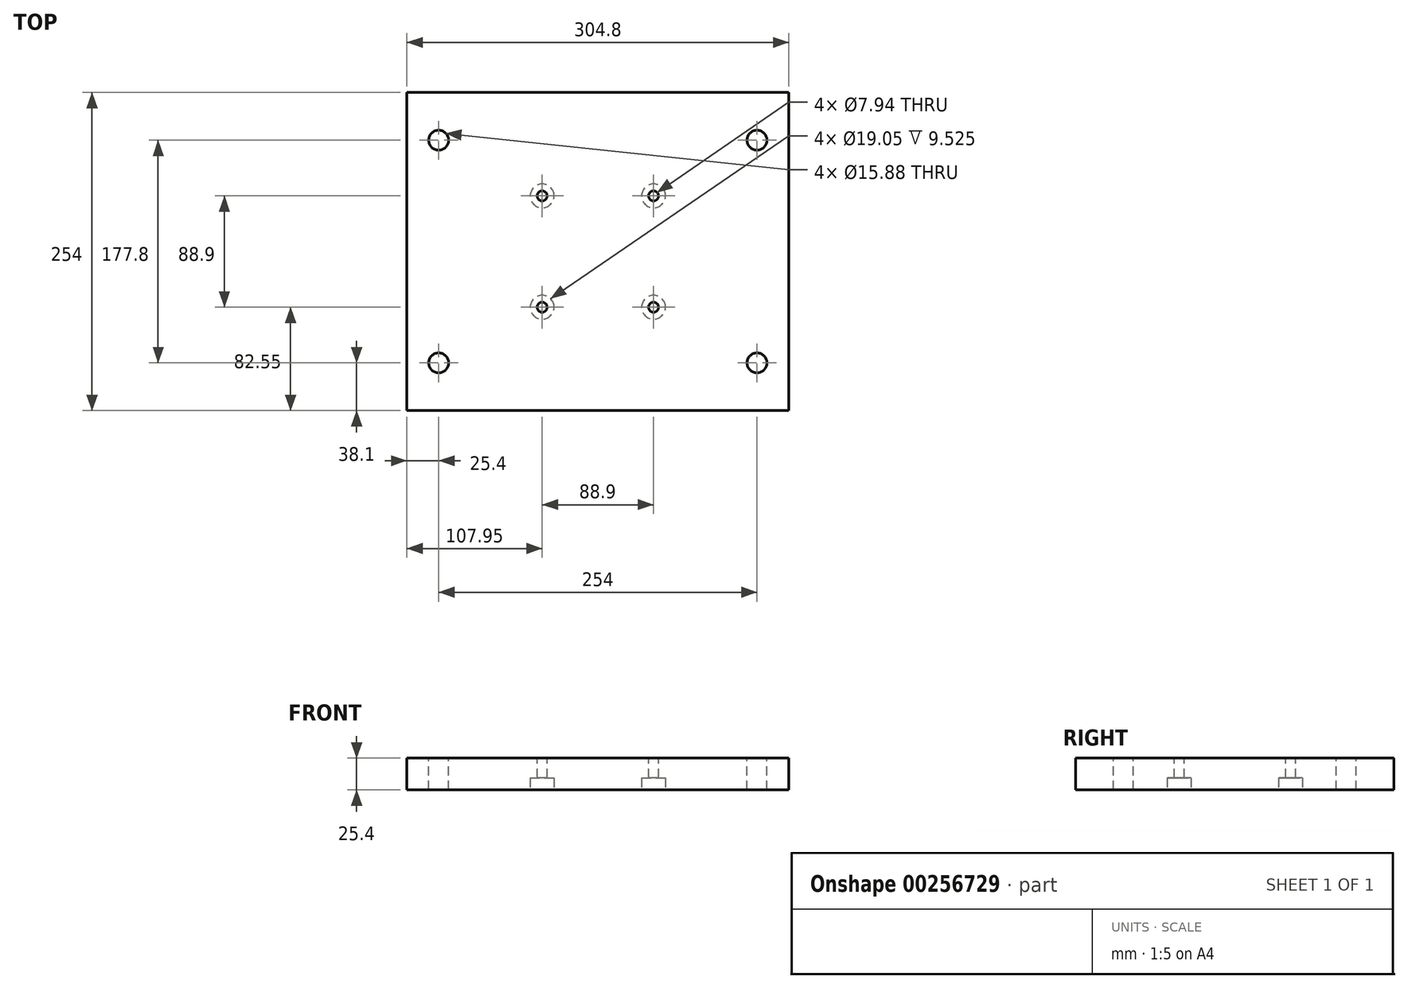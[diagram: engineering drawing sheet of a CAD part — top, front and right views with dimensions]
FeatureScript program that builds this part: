
annotation { "Feature Type Name" : "Feature", "Feature Type Description" : "" }
export const myFeature = defineFeature(function(context is Context, id is Id, definition is map)
    precondition{}
    {
        {
            var Q0;
            Q0=qCreatedBy(makeId("Top.planeOp"),FACE);
            var sketch = newSketch(context, id + "F0", { "sketchPlane" : qUnion([Q0])});
            skLineSegment(sketch, "E0.bottom", {"start": v(0, 0) * mm, "end": v(304.8, 0) * mm});
            skLineSegment(sketch, "E0.top", {"start": v(0, 254) * mm, "end": v(304.8, 254) * mm});
            skLineSegment(sketch, "E0.left", {"start": v(0, 0) * mm, "end": v(0, 254) * mm});
            skLineSegment(sketch, "E0.right", {"start": v(304.8, 0) * mm, "end": v(304.8, 254) * mm});
            skSolve(sketch);
        }
        {
            var Q0;
            Q0=makeQuery(id+"F0.imprint","IMPRINT",FACE,{"disambiguationData":[TD([[makeQuery(id+"F0.imprint","IMPRINT",EDGE,{"derivedFrom":sQuery(id+"F0.wireOp",EDGE,"E0.bottom")}),1.0]])]});
            extrude(context, id + "F1", {"entities" : qUnion([Q0]), "oppositeDirection" : true, "depth" : 25.4 * mm});
        }
        {
            var Q0;
            Q0=makeQuery(id+"F1.opExtrude","CAP_FACE",FACE,{"disambiguationData":[OSD([sQuery(id+"F0.wireOp",EDGE,"E0.bottom"),sQuery(id+"F0.wireOp",EDGE,"E0.top"),sQuery(id+"F0.wireOp",EDGE,"E0.left"),sQuery(id+"F0.wireOp",EDGE,"E0.right")])],"isStart":true});
            var sketch = newSketch(context, id + "F2", { "sketchPlane" : qUnion([Q0])});
            skLineSegment(sketch, "E1.bottom", {"start": v(196.85, 171.45) * mm, "end": v(107.95, 171.45) * mm, "construction": true});
            skLineSegment(sketch, "E1.top", {"start": v(196.85, 82.55) * mm, "end": v(107.95, 82.55) * mm, "construction": true});
            skLineSegment(sketch, "E1.left", {"start": v(196.85, 171.45) * mm, "end": v(196.85, 82.55) * mm, "construction": true});
            skLineSegment(sketch, "E1.right", {"start": v(107.95, 171.45) * mm, "end": v(107.95, 82.55) * mm, "construction": true});
            skPoint(sketch, "E1.middle", {"position": v(152.4, 127) * mm});
            skCircle(sketch, "E2", {"center": v(107.95, 171.45) * mm, "radius": 3.97 * mm});
            skCircle(sketch, "E3", {"center": v(196.85, 171.45) * mm, "radius": 3.97 * mm});
            skCircle(sketch, "E4", {"center": v(107.95, 82.55) * mm, "radius": 3.97 * mm});
            skCircle(sketch, "E5", {"center": v(196.85, 82.55) * mm, "radius": 3.97 * mm});
            skPoint(sketch, "E6.endSnap0", {"position": v(152.4, 0) * mm});
            skLineSegment(sketch, "E7", {"start": v(0, 254) * mm, "end": v(304.8, 0) * mm, "construction": true});
            skLineSegment(sketch, "E8", {"start": v(304.8, 0) * mm, "end": v(304.8, 254) * mm, "construction": true});
            skLineSegment(sketch, "E9", {"start": v(304.8, 254) * mm, "end": v(0, 0) * mm, "construction": true});
            skLineSegment(sketch, "E10", {"start": v(152.4, 254) * mm, "end": v(152.4, 0) * mm, "construction": true});
            skLineSegment(sketch, "E11", {"start": v(0, 127) * mm, "end": v(304.8, 127) * mm, "construction": true});
            skLineSegment(sketch, "E12.bottom", {"start": v(279.4, 38.1) * mm, "end": v(25.4, 38.1) * mm, "construction": true});
            skLineSegment(sketch, "E12.top", {"start": v(279.4, 215.9) * mm, "end": v(25.4, 215.9) * mm, "construction": true});
            skLineSegment(sketch, "E12.left", {"start": v(279.4, 38.1) * mm, "end": v(279.4, 215.9) * mm, "construction": true});
            skLineSegment(sketch, "E12.right", {"start": v(25.4, 38.1) * mm, "end": v(25.4, 215.9) * mm, "construction": true});
            skCircle(sketch, "E13", {"center": v(25.4, 215.9) * mm, "radius": 7.94 * mm});
            skCircle(sketch, "E14", {"center": v(279.4, 215.9) * mm, "radius": 7.94 * mm});
            skCircle(sketch, "E15", {"center": v(279.4, 38.1) * mm, "radius": 7.94 * mm});
            skCircle(sketch, "E16", {"center": v(25.4, 38.1) * mm, "radius": 7.94 * mm});
            skSolve(sketch);
        }
        {
            var Q0;
            Q0=makeQuery(id+"F2.imprint","IMPRINT",FACE,{"disambiguationData":[TD([[makeQuery(id+"F2.imprint","IMPRINT",EDGE,{"derivedFrom":sQuery(id+"F2.wireOp",EDGE,"E2")}),1.0]])]});
            var Q1;
            Q1=makeQuery(id+"F2.imprint","IMPRINT",FACE,{"disambiguationData":[TD([[makeQuery(id+"F2.imprint","IMPRINT",EDGE,{"derivedFrom":sQuery(id+"F2.wireOp",EDGE,"E3")}),1.0]])]});
            var Q2;
            Q2=makeQuery(id+"F2.imprint","IMPRINT",FACE,{"disambiguationData":[TD([[makeQuery(id+"F2.imprint","IMPRINT",EDGE,{"derivedFrom":sQuery(id+"F2.wireOp",EDGE,"E5")}),1.0]])]});
            var Q3;
            Q3=makeQuery(id+"F2.imprint","IMPRINT",FACE,{"disambiguationData":[TD([[makeQuery(id+"F2.imprint","IMPRINT",EDGE,{"derivedFrom":sQuery(id+"F2.wireOp",EDGE,"E4")}),1.0]])]});
            extrude(context, id + "F3", {"entities" : qUnion([Q0, Q1, Q2, Q3]), "operationType" : NewBodyOperationType.REMOVE, "oppositeDirection" : true, "depth" : 25.4 * mm});
        }
        {
            var Q0;
            Q0=makeQuery(id+"F1.opExtrude","CAP_FACE",FACE,{"disambiguationData":[OSD([sQuery(id+"F0.wireOp",EDGE,"E0.bottom"),sQuery(id+"F0.wireOp",EDGE,"E0.top"),sQuery(id+"F0.wireOp",EDGE,"E0.left"),sQuery(id+"F0.wireOp",EDGE,"E0.right")])],"isStart":false});
            var sketch = newSketch(context, id + "F4", { "sketchPlane" : qUnion([Q0])});
            skCircle(sketch, "E17", {"center": v(107.95, -82.55) * mm, "radius": 9.53 * mm});
            skCircle(sketch, "E18", {"center": v(196.85, -82.55) * mm, "radius": 9.53 * mm});
            skCircle(sketch, "E19", {"center": v(107.95, -171.45) * mm, "radius": 9.53 * mm});
            skCircle(sketch, "E20", {"center": v(196.85, -171.45) * mm, "radius": 9.53 * mm});
            skSolve(sketch);
        }
        {
            var Q0;
            Q0=makeQuery(id+"F4.imprint","IMPRINT",FACE,{"disambiguationData":[TD([[makeQuery(id+"F4.imprint","IMPRINT",EDGE,{"derivedFrom":makeQuery(id+"F3.boolean.opBoolean","COPY",EDGE,{"derivedFrom":makeQuery(id+"F3.opExtrude","CAP_EDGE",EDGE,{"disambiguationData":[OSD([sQuery(id+"F2.wireOp",EDGE,"E2")])],"isStart":false})})}),-1.0]])]});
            var Q1;
            Q1=makeQuery(id+"F4.imprint","IMPRINT",FACE,{"disambiguationData":[TD([[makeQuery(id+"F4.imprint","IMPRINT",EDGE,{"derivedFrom":makeQuery(id+"F3.boolean.opBoolean","COPY",EDGE,{"derivedFrom":makeQuery(id+"F3.opExtrude","CAP_EDGE",EDGE,{"disambiguationData":[OSD([sQuery(id+"F2.wireOp",EDGE,"E3")])],"isStart":false})})}),-1.0]])]});
            var Q2;
            Q2=makeQuery(id+"F4.imprint","IMPRINT",FACE,{"disambiguationData":[TD([[makeQuery(id+"F4.imprint","IMPRINT",EDGE,{"derivedFrom":makeQuery(id+"F3.boolean.opBoolean","COPY",EDGE,{"derivedFrom":makeQuery(id+"F3.opExtrude","CAP_EDGE",EDGE,{"disambiguationData":[OSD([sQuery(id+"F2.wireOp",EDGE,"E4")])],"isStart":false})})}),-1.0]])]});
            var Q3;
            Q3=makeQuery(id+"F4.imprint","IMPRINT",FACE,{"disambiguationData":[TD([[makeQuery(id+"F4.imprint","IMPRINT",EDGE,{"derivedFrom":makeQuery(id+"F3.boolean.opBoolean","COPY",EDGE,{"derivedFrom":makeQuery(id+"F3.opExtrude","CAP_EDGE",EDGE,{"disambiguationData":[OSD([sQuery(id+"F2.wireOp",EDGE,"E5")])],"isStart":false})})}),-1.0]])]});
            var Q4;
            Q4=makeQuery(id+"F4.imprint","IMPRINT",FACE,{"disambiguationData":[TD([[makeQuery(id+"F4.imprint","IMPRINT",EDGE,{"derivedFrom":sQuery(id+"F4.wireOp",EDGE,"E17")}),1.0]])]});
            var Q5;
            Q5=makeQuery(id+"F4.imprint","IMPRINT",FACE,{"disambiguationData":[TD([[makeQuery(id+"F4.imprint","IMPRINT",EDGE,{"derivedFrom":sQuery(id+"F4.wireOp",EDGE,"E18")}),1.0]])]});
            var Q6;
            Q6=makeQuery(id+"F4.imprint","IMPRINT",FACE,{"disambiguationData":[TD([[makeQuery(id+"F4.imprint","IMPRINT",EDGE,{"derivedFrom":sQuery(id+"F4.wireOp",EDGE,"E20")}),1.0]])]});
            var Q7;
            Q7=makeQuery(id+"F4.imprint","IMPRINT",FACE,{"disambiguationData":[TD([[makeQuery(id+"F4.imprint","IMPRINT",EDGE,{"derivedFrom":sQuery(id+"F4.wireOp",EDGE,"E19")}),1.0]])]});
            extrude(context, id + "F5", {"entities" : qUnion([Q0, Q1, Q2, Q3, Q4, Q5, Q6, Q7]), "operationType" : NewBodyOperationType.REMOVE, "oppositeDirection" : true, "depth" : 9.52 * mm});
        }
        {
            var Q0;
            Q0 = qSketchRegion(id + "F2", true);
            extrude(context, id + "F6", {"entities" : qUnion([Q0]), "operationType" : NewBodyOperationType.REMOVE, "oppositeDirection" : true, "depth" : 25.4 * mm});
        }
    });
